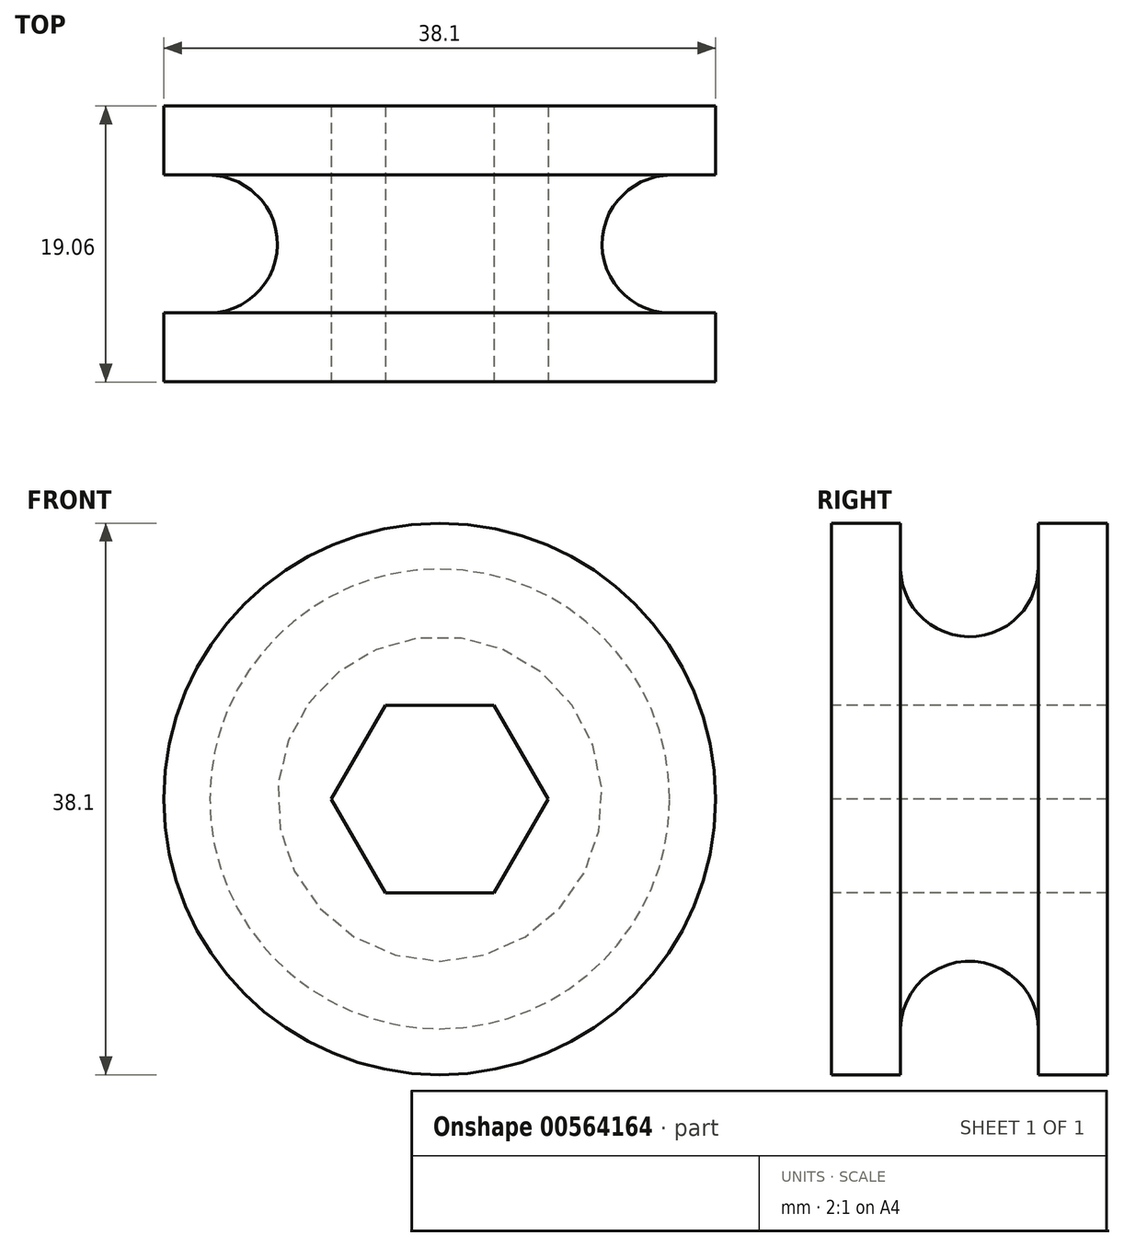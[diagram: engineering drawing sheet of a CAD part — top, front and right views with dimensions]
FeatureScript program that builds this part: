
annotation { "Feature Type Name" : "Feature", "Feature Type Description" : "" }
export const myFeature = defineFeature(function(context is Context, id is Id, definition is map)
    precondition{}
    {
        {
            var Q0;
            Q0=qCreatedBy(makeId("Front.planeOp"),FACE);
            var sketch = newSketch(context, id + "F0", { "sketchPlane" : qUnion([Q0])});
            skCircle(sketch, "E0.cCircle", {"center": v(0, 0) * mm, "radius": 6.48 * mm, "construction": true});
            skLineSegment(sketch, "E0.0", {"start": v(-3.74, 6.48) * mm, "end": v(3.74, 6.48) * mm});
            skLineSegment(sketch, "E0.1", {"start": v(3.74, 6.48) * mm, "end": v(7.48, 0) * mm});
            skLineSegment(sketch, "E0.2", {"start": v(7.48, 0) * mm, "end": v(3.74, -6.48) * mm});
            skLineSegment(sketch, "E0.3", {"start": v(3.74, -6.48) * mm, "end": v(-3.74, -6.48) * mm});
            skLineSegment(sketch, "E0.4", {"start": v(-3.74, -6.48) * mm, "end": v(-7.48, 0) * mm});
            skLineSegment(sketch, "E0.5", {"start": v(-7.48, 0) * mm, "end": v(-3.74, 6.48) * mm});
            skPoint(sketch, "E0.0.midPoint", {"position": v(0, 6.48) * mm});
            skSolve(sketch);
        }
        {
            var Q0;
            Q0=qCreatedBy(makeId("Right.planeOp"),FACE);
            var sketch = newSketch(context, id + "F1", { "sketchPlane" : qUnion([Q0])});
            skLineSegment(sketch, "E1.0", {"start": v(0, -19.05) * mm, "end": v(0, 19.05) * mm, "construction": true});
            skLineSegment(sketch, "E2", {"start": v(-4.76, 19.05) * mm, "end": v(-9.52, 19.05) * mm});
            skLineSegment(sketch, "E3", {"start": v(-9.52, 19.05) * mm, "end": v(-9.53, 0) * mm});
            skLineSegment(sketch, "E4.MirrorCS", {"start": v(4.76, 19.05) * mm, "end": v(9.53, 19.05) * mm});
            skLineSegment(sketch, "E5.MirrorCS", {"start": v(9.53, 19.05) * mm, "end": v(9.52, 0) * mm});
            skPoint(sketch, "E6.orphan", {"position": v(0, 19.05) * mm});
            skLineSegment(sketch, "E7", {"start": v(-9.52, 0) * mm, "end": v(9.52, 0) * mm});
            skLineSegment(sketch, "E8", {"start": v(-4.76, 19.05) * mm, "end": v(-4.76, 15.88) * mm});
            skLineSegment(sketch, "E9", {"start": v(4.76, 19.05) * mm, "end": v(4.76, 15.97) * mm});
            skArc(sketch, "E10", {"start": v(-4.76, 15.88) * mm, "mid": v(0.05, 11.2) * mm, "end": v(4.76, 15.97) * mm});
            skSolve(sketch);
        }
        {
            var Q0;
            Q0 = qSketchRegion(id + "F1", true);
            var Q1;
            Q1=sQuery(id+"F1.wireOp",EDGE,"E7");
            revolve(context, id + "F2", {"entities" : qUnion([Q0]), "axis" : qUnion([Q1]), "revolveType" : RevolveType.FULL});
        }
        {
            var Q0;
            Q0 = qSketchRegion(id + "F0", true);
            extrude(context, id + "F3", {"entities" : qUnion([Q0]), "operationType" : NewBodyOperationType.REMOVE, "oppositeDirection" : true, "depth" : 25.4 * mm, "offsetDistance" : 25.4 * mm, "symmetric" : true});
        }
    });
